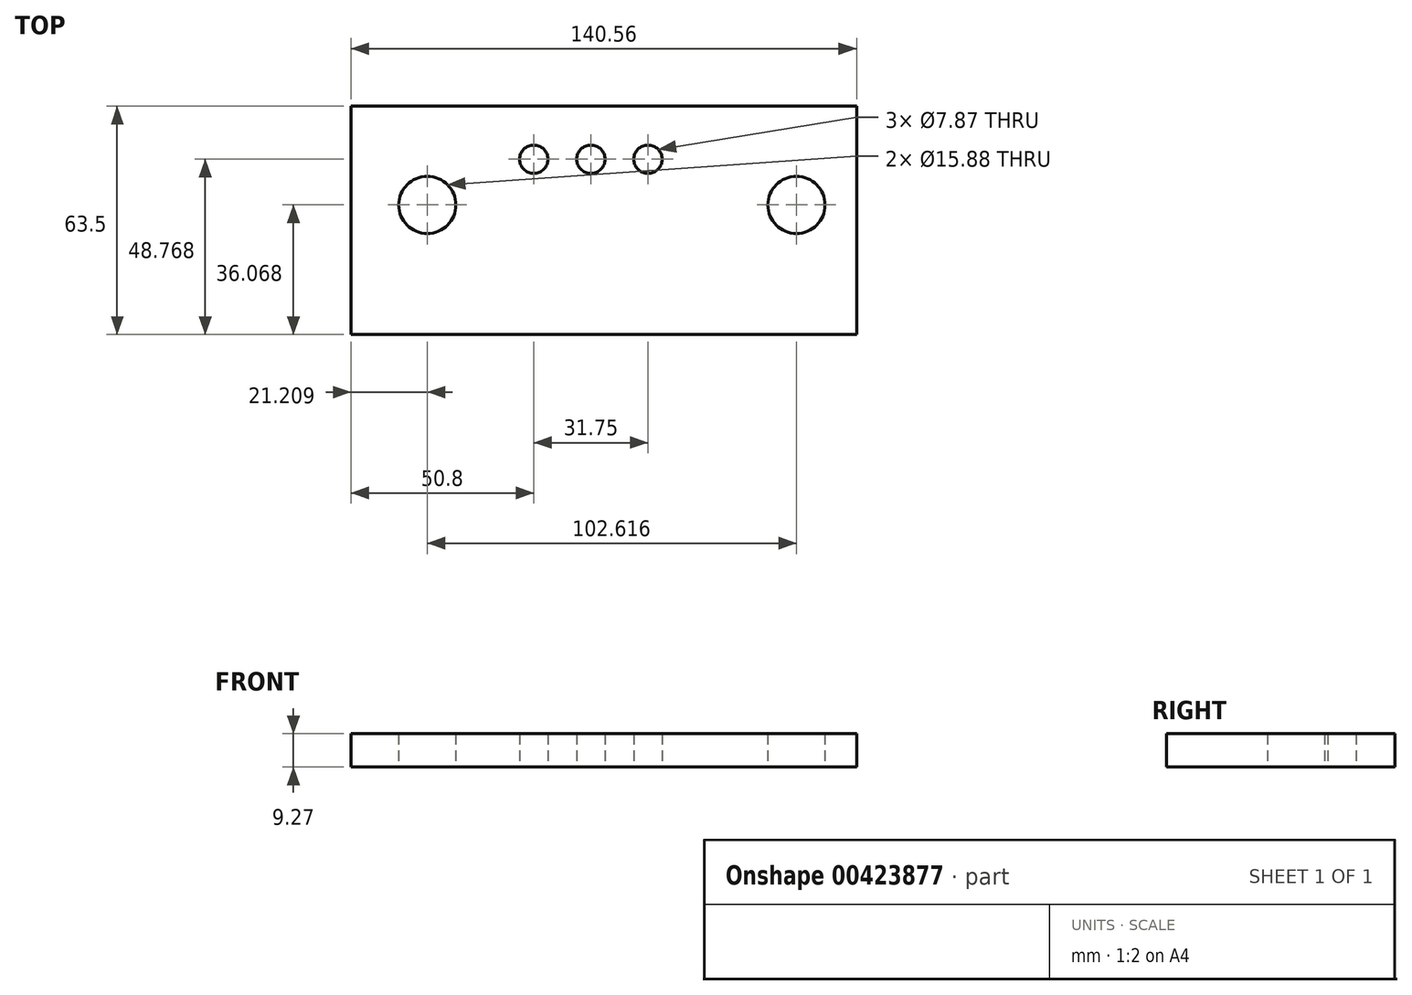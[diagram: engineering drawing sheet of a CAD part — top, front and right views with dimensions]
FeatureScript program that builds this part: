
annotation { "Feature Type Name" : "Feature", "Feature Type Description" : "" }
export const myFeature = defineFeature(function(context is Context, id is Id, definition is map)
    precondition{}
    {
        {
            var Q0;
            Q0=qCreatedBy(makeId("Top.planeOp"),FACE);
            var sketch = newSketch(context, id + "F0", { "sketchPlane" : qUnion([Q0])});
            skLineSegment(sketch, "E0.bottom", {"start": v(0, 0) * mm, "end": v(140.56, 0) * mm});
            skLineSegment(sketch, "E0.top", {"start": v(0, 63.5) * mm, "end": v(140.56, 63.5) * mm});
            skLineSegment(sketch, "E0.left", {"start": v(0, 0) * mm, "end": v(0, 63.5) * mm});
            skLineSegment(sketch, "E0.right", {"start": v(140.56, 0) * mm, "end": v(140.56, 63.5) * mm});
            skLineSegment(sketch, "E1", {"start": v(0, 36.07) * mm, "end": v(21.2, 36.07) * mm, "construction": true});
            skCircle(sketch, "E2", {"center": v(21.2, 36.07) * mm, "radius": 7.94 * mm});
            skLineSegment(sketch, "E3", {"start": v(0, 48.77) * mm, "end": v(50.8, 48.77) * mm, "construction": true});
            skCircle(sketch, "E4", {"center": v(50.8, 48.77) * mm, "radius": 3.94 * mm});
            skCircle(sketch, "E5", {"center": v(66.67, 48.77) * mm, "radius": 3.94 * mm});
            skCircle(sketch, "E6", {"center": v(82.55, 48.77) * mm, "radius": 3.94 * mm});
            skLineSegment(sketch, "E7", {"start": v(0, 36.07) * mm, "end": v(123.83, 36.07) * mm, "construction": true});
            skCircle(sketch, "E8", {"center": v(123.83, 36.07) * mm, "radius": 7.94 * mm});
            skSolve(sketch);
        }
        {
            var Q0;
            Q0=makeQuery(id+"F0.imprint","IMPRINT",FACE,{"disambiguationData":[TD([[makeQuery(id+"F0.imprint","IMPRINT",EDGE,{"derivedFrom":sQuery(id+"F0.wireOp",EDGE,"E0.bottom")}),1.0]])]});
            var Q1;
            Q1 = qConstructionFilter(qBodyType(qCreatedBy(id + "F0" ,EDGE), BodyType.WIRE), ConstructionObject.NO);
            extrude(context, id + "F1", {"entities" : qUnion([Q0]), "surfaceEntities" : qUnion([Q1]), "depth" : 9.27 * mm});
        }
    });
